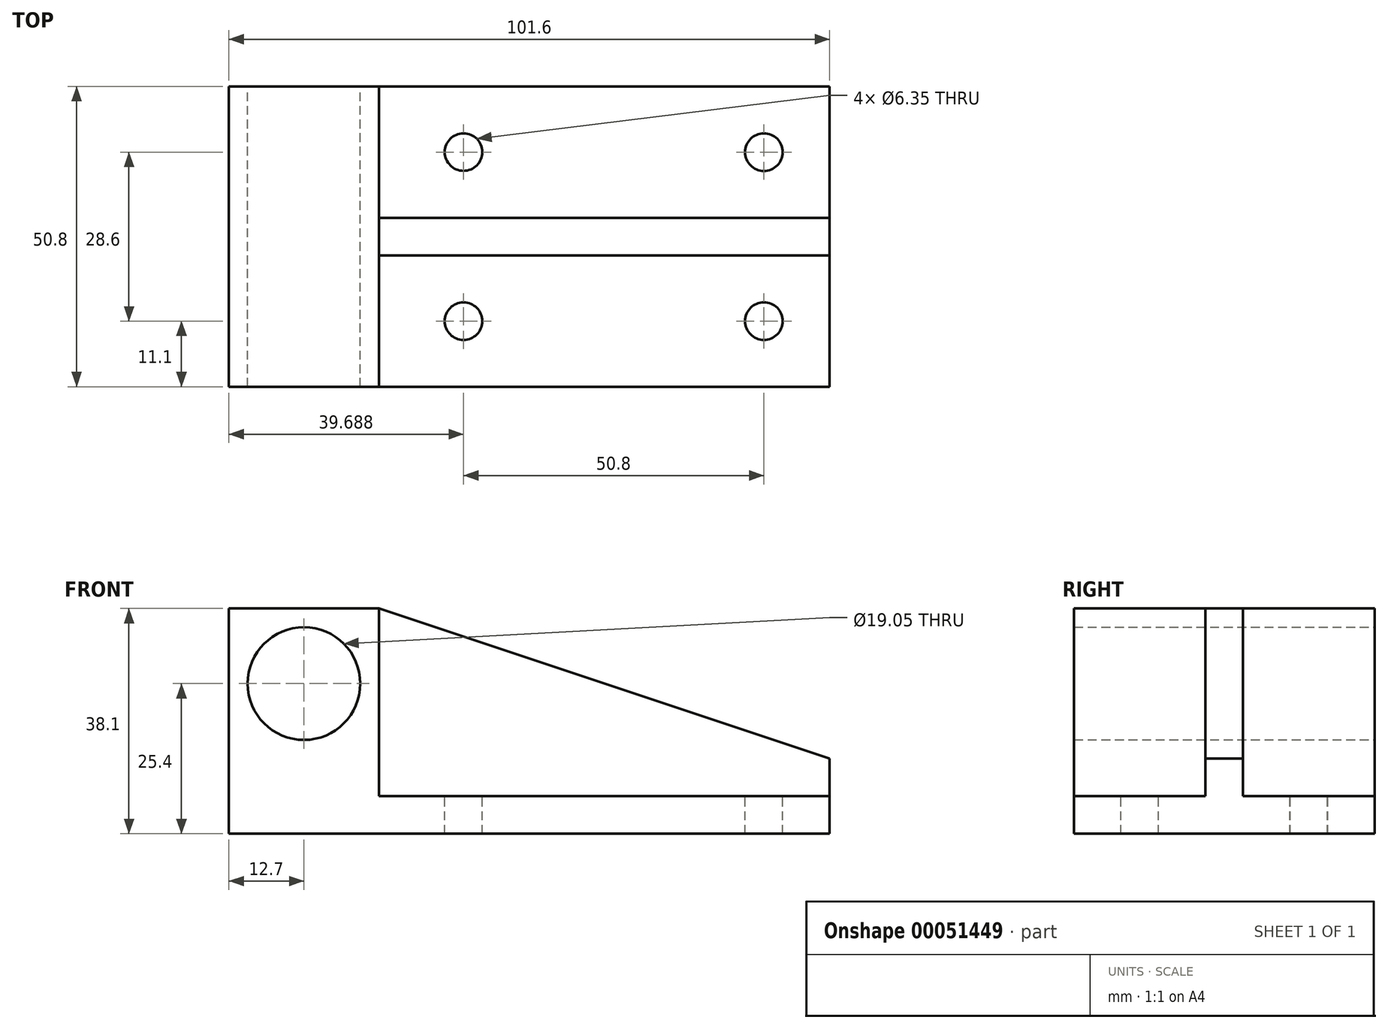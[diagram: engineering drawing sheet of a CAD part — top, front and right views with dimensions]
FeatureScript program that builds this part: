
annotation { "Feature Type Name" : "Feature", "Feature Type Description" : "" }
export const myFeature = defineFeature(function(context is Context, id is Id, definition is map)
    precondition{}
    {
        {
            var Q0;
            Q0=qCreatedBy(makeId("Front.planeOp"),FACE);
            var sketch = newSketch(context, id + "F0", { "sketchPlane" : qUnion([Q0])});
            skLineSegment(sketch, "E0.rect.bottom", {"start": v(-25.4, 19.05) * mm, "end": v(-50.8, 19.05) * mm});
            skLineSegment(sketch, "E0.rect.top", {"start": v(50.8, -19.05) * mm, "end": v(-50.8, -19.05) * mm});
            skLineSegment(sketch, "E0.rect.left", {"start": v(50.8, -12.7) * mm, "end": v(50.8, -19.05) * mm});
            skLineSegment(sketch, "E0.rect.right", {"start": v(-50.8, 19.05) * mm, "end": v(-50.8, -19.05) * mm});
            skPoint(sketch, "E0.rect.middle", {"position": v(0, 0) * mm});
            skLineSegment(sketch, "E1", {"start": v(-25.4, 19.05) * mm, "end": v(-25.4, -12.7) * mm});
            skLineSegment(sketch, "E2", {"start": v(-25.4, -12.7) * mm, "end": v(50.8, -12.7) * mm});
            skPoint(sketch, "E3.orphan", {"position": v(50.8, 19.05) * mm});
            skCircle(sketch, "E4", {"center": v(-38.1, 6.35) * mm, "radius": 9.53 * mm});
            skSolve(sketch);
        }
        {
            var Q0;
            Q0 = qSketchRegion(id + "F0", true);
            extrude(context, id + "F1", {"entities" : qUnion([Q0]), "depth" : 25.4 * mm});
        }
        {
            var Q0;
            Q0=qCreatedBy(makeId("Front.planeOp"),FACE);
            var sketch = newSketch(context, id + "F2", { "sketchPlane" : qUnion([Q0])});
            skLineSegment(sketch, "E5", {"start": v(-25.4, 19.05) * mm, "end": v(50.8, -6.35) * mm});
            skLineSegment(sketch, "E6", {"start": v(50.8, -6.35) * mm, "end": v(50.8, -12.7) * mm});
            skLineSegment(sketch, "E7", {"start": v(50.8, -12.7) * mm, "end": v(-25.4, -12.7) * mm});
            skLineSegment(sketch, "E8", {"start": v(-25.4, -12.7) * mm, "end": v(-25.4, 19.05) * mm});
            skSolve(sketch);
        }
        {
            var Q0;
            Q0 = qSketchRegion(id + "F2", true);
            extrude(context, id + "F3", {"entities" : qUnion([Q0]), "operationType" : NewBodyOperationType.ADD, "depth" : 3.17 * mm});
        }
        {
            var Q0;
            {var subQ0=sQuery(id+"F2.wireOp",EDGE,"E6");var subQ3=sQuery(id+"F0.wireOp",EDGE,"E2");Q0=makeQuery(id+"F3.boolean.opBoolean","SPLIT",FACE,{"disambiguationData":[TD([makeQuery(id+"F3.opExtrude","CAP_FACE",FACE,{"disambiguationData":[OSD([sQuery(id+"F2.wireOp",EDGE,"E5"),subQ0,sQuery(id+"F2.wireOp",EDGE,"E7"),sQuery(id+"F2.wireOp",EDGE,"E8")])],"isStart":false})])],"derivedFrom":makeQuery(id+"F1.opExtrude","SWEPT_FACE",FACE,{"disambiguationData":[OSD([subQ3])]})});}
            var sketch = newSketch(context, id + "F4", { "sketchPlane" : qUnion([Q0])});
            skCircle(sketch, "E9", {"center": v(39.69, -14.29) * mm, "radius": 3.18 * mm});
            skCircle(sketch, "E10", {"center": v(-11.11, -14.3) * mm, "radius": 3.18 * mm});
            skSolve(sketch);
        }
        {
            var Q0;
            Q0 = qSketchRegion(id + "F4", true);
            extrude(context, id + "F5", {"entities" : qUnion([Q0]), "operationType" : NewBodyOperationType.REMOVE, "oppositeDirection" : true, "depth" : 25.4 * mm});
        }
        {
            var Q0;
            Q0=makeQuery(id+"F1.opExtrude","SWEPT_BODY",BODY,{"disambiguationData":[OSD([sQuery(id+"F0.wireOp",EDGE,"E0.rect.bottom"),sQuery(id+"F0.wireOp",EDGE,"E0.rect.top"),sQuery(id+"F0.wireOp",EDGE,"E0.rect.left"),sQuery(id+"F0.wireOp",EDGE,"E0.rect.right"),sQuery(id+"F0.wireOp",EDGE,"E1"),sQuery(id+"F0.wireOp",EDGE,"E2"),sQuery(id+"F0.wireOp",EDGE,"E4")])]});
            var Q1;
            Q1=qCreatedBy(makeId("Front.planeOp"),FACE);
            mirror(context, id + "F6", {"operationType" : NewBodyOperationType.ADD, "entities" : qUnion([Q0]), "mirrorPlane" : qUnion([Q1])});
        }
    });
